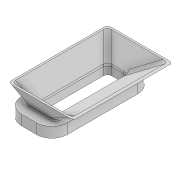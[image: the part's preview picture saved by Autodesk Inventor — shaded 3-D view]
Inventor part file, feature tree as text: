
AUTODESK INVENTOR PART (.ipt)
format: ipt  version: 2022 (Build 260153000, 153)  size: 568,832 bytes
history: native  units: mm
features: fillet x5, sketch x5, projected_geometry x5, extrude x3, plane x1, loft x1, shell x1
ambient origin geometry x8: Origin, YZ Plane, XZ Plane, XY Plane, X Axis, Y Axis, Z Axis, Center Point
bodies: Solid1 (feature_tree)
feature tree (21):
  extrude  "Extrusion1"  Depth=55.0mm
  plane  "Work Plane1"
  loft  "Loft1"
  shell  "Shell1"  Thickness=50.0mm
  fillet  "Fillet1"  Radius=20.0mm
  fillet  "Fillet2"  Radius=50.0mm
  fillet  "Fillet3"  Radius=4.0mm
  fillet  "Fillet4"  Radius=4.0mm
  extrude  "Extrusion2"  Depth=4.0mm
  extrude  "Extrusion3"  TaperAngle=0.0deg  [1 undecoded]
  fillet  "Fillet5"  Radius=4.0mm
  sketch  "Sketch1"  dims[d0=185.0mm d1=55.0mm]
  sketch  "Sketch2"  dims[d2=4.0mm d3=20.0mm d4=0.0mm d5=50.0mm d6=20.0mm d7=50.0mm d8=4.0mm d9=4.0mm]
  projected_geometry  "Projected Loop1"
  sketch  "Sketch3"  dims[d10=4.0mm d11=4.0mm]
  projected_geometry  "Projected Loop2"
  sketch  "Sketch4"  dims[d12=0.0mm d13=90.0deg d14=0.0mm d15=90.0deg d16=4.0mm]
  projected_geometry  "Projected Loop3"
  sketch  "Sketch5"  dims[d17=10.0mm d18=10.0mm d19=10.0mm d20=10.0mm d21=24.0mm d22=2.0mm d23=20.0mm d24=0.0mm d25=4.0mm d26=0.0mm d27=2.0mm]
  projected_geometry  "Projected Loop4"
  projected_geometry  "Project Cut Edges1"
note: 1 required parameter value undecoded (feature->parameter linkage not recoverable at this tier; creation-order binding heuristic only, values carry confidence <= 0.55)
